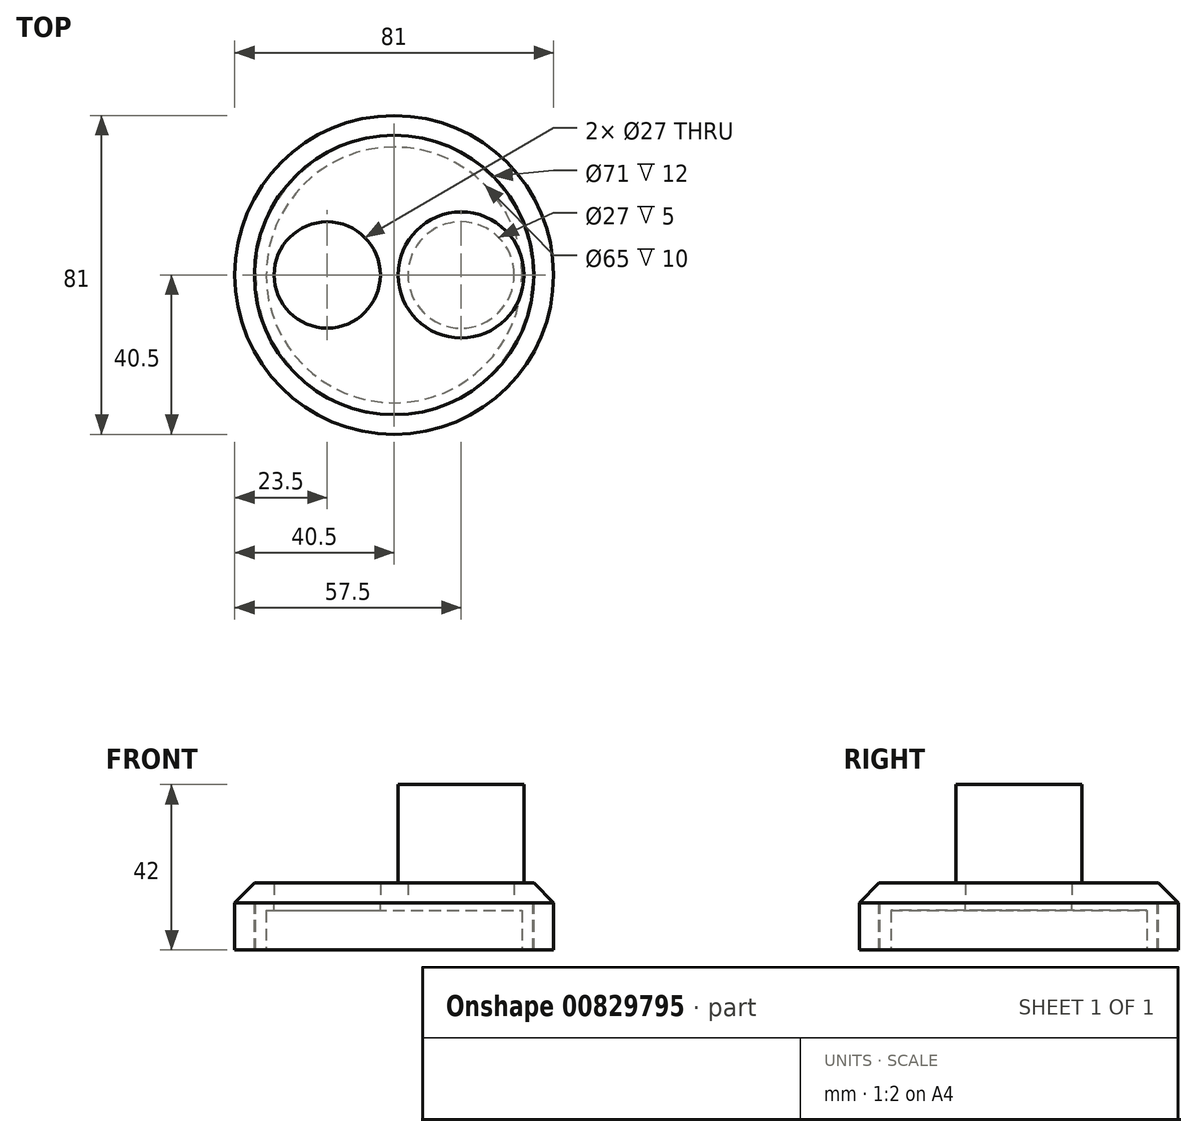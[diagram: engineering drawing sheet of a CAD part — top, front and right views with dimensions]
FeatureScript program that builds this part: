
annotation { "Feature Type Name" : "Feature", "Feature Type Description" : "" }
export const myFeature = defineFeature(function(context is Context, id is Id, definition is map)
    precondition{}
    {
        {
            var Q0;
            Q0=qCreatedBy(makeId("Front.planeOp"),FACE);
            var sketch = newSketch(context, id + "F0", { "sketchPlane" : qUnion([Q0])});
            skLineSegment(sketch, "E0", {"start": v(-40.5, 0) * mm, "end": v(-40.5, 17) * mm});
            skLineSegment(sketch, "E1", {"start": v(-40.5, 17) * mm, "end": v(0, 17) * mm});
            skLineSegment(sketch, "E2", {"start": v(0, 17) * mm, "end": v(0, 12) * mm});
            skLineSegment(sketch, "E3", {"start": v(0, 12) * mm, "end": v(-35.5, 12) * mm});
            skLineSegment(sketch, "E4", {"start": v(-35.5, 12) * mm, "end": v(-35.5, 0) * mm});
            skLineSegment(sketch, "E5", {"start": v(-35.5, 0) * mm, "end": v(-40.5, 0) * mm});
            skSolve(sketch);
        }
        {
            var Q0;
            Q0=makeQuery(id+"F0.imprint","IMPRINT",FACE,{"disambiguationData":[TD([[makeQuery(id+"F0.imprint","IMPRINT",EDGE,{"derivedFrom":sQuery(id+"F0.wireOp",EDGE,"E0")}),-1.0]])]});
            var Q1;
            Q1=sQuery(id+"F0.wireOp",EDGE,"E2");
            revolve(context, id + "F1", {"surfaceOperationType" : NewSurfaceOperationType.NEW, "entities" : qUnion([Q0]), "axis" : qUnion([Q1]), "revolveType" : RevolveType.FULL});
        }
        {
            var Q0;
            Q0=makeQuery(id+"F1.opRevolve","SWEPT_FACE",FACE,{"disambiguationData":[OSD([sQuery(id+"F0.wireOp",EDGE,"E3")])]});
            var sketch = newSketch(context, id + "F2", { "sketchPlane" : qUnion([Q0])});
            skCircle(sketch, "E6", {"center": v(0, 0) * mm, "radius": 17 * mm, "construction": true});
            skLineSegment(sketch, "E7", {"start": v(0, 0) * mm, "end": v(-17, 0) * mm, "construction": true});
            skLineSegment(sketch, "E8", {"start": v(0, 0) * mm, "end": v(0, 17) * mm, "construction": true});
            skCircle(sketch, "E9", {"center": v(-17, 0) * mm, "radius": 13.5 * mm});
            skCircle(sketch, "E10.MirrorC", {"center": v(17, 0) * mm, "radius": 13.5 * mm});
            skSolve(sketch);
        }
        {
            var Q0;
            Q0 = qSketchRegion(id + "F2", true);
            extrude(context, id + "F3", {"entities" : qUnion([Q0]), "operationType" : NewBodyOperationType.REMOVE, "oppositeDirection" : true, "depth" : 25 * mm, "offsetDistance" : 25 * mm});
        }
        {
            var Q0;
            Q0=makeQuery(id+"F1.opRevolve","SWEPT_EDGE",EDGE,{"disambiguationData":[OSD([sQuery(id+"F0.wireOp",EDGE,"E0"),sQuery(id+"F0.wireOp",EDGE,"E1")])]});
            chamfer(context, id + "F4", {"entities" : qUnion([Q0]), "width" : 5 * mm, "tangentPropagation" : true});
        }
        {
            var Q0;
            Q0=makeQuery(id+"F1.opRevolve","SWEPT_FACE",FACE,{"disambiguationData":[OSD([sQuery(id+"F0.wireOp",EDGE,"E3")])]});
            var sketch = newSketch(context, id + "F5", { "sketchPlane" : qUnion([Q0])});
            skCircle(sketch, "E11", {"center": v(0, 0) * mm, "radius": 35.25 * mm});
            skCircle(sketch, "E12.0", {"center": v(-17, 0) * mm, "radius": 13.5 * mm});
            skSolve(sketch);
        }
        {
            var Q0;
            Q0=makeQuery(id+"F5.imprint","IMPRINT",FACE,{"disambiguationData":[TD([[makeQuery(id+"F5.imprint","IMPRINT",EDGE,{"derivedFrom":sQuery(id+"F5.wireOp",EDGE,"E11")}),1.0]])]});
            var Q1;
            Q1 = qSketchRegion(id + "F5", true);
            extrude(context, id + "F6", {"entities" : qUnion([Q0, Q1]), "depth" : 12 * mm, "offsetDistance" : 25 * mm});
        }
        {
            var Q0;
            Q0=makeQuery(id+"F6.opExtrude","CAP_FACE",FACE,{"disambiguationData":[OSD([sQuery(id+"F5.wireOp",EDGE,"E11"),sQuery(id+"F5.wireOp",EDGE,"E12.0")])],"isStart":false});
            var sketch = newSketch(context, id + "F7", { "sketchPlane" : qUnion([Q0])});
            skCircle(sketch, "E13", {"center": v(0, 0) * mm, "radius": 32.5 * mm});
            skSolve(sketch);
        }
        {
            var Q0;
            Q0 = qSketchRegion(id + "F7", true);
            var Q1;
            Q1=makeQuery(id+"F7.imprint","IMPRINT",FACE,{"disambiguationData":[TD([[makeQuery(id+"F7.imprint","IMPRINT",EDGE,{"derivedFrom":sQuery(id+"F7.wireOp",EDGE,"E13")}),1.0]])]});
            extrude(context, id + "F8", {"entities" : qUnion([Q0, Q1]), "operationType" : NewBodyOperationType.REMOVE, "oppositeDirection" : true, "depth" : 10 * mm, "offsetDistance" : 25 * mm});
        }
        {
            var Q0;
            Q0=makeQuery(id+"F1.opRevolve","SWEPT_FACE",FACE,{"disambiguationData":[OSD([sQuery(id+"F0.wireOp",EDGE,"E1")])]});
            var sketch = newSketch(context, id + "F9", { "sketchPlane" : qUnion([Q0])});
            skCircle(sketch, "E14.0", {"center": v(17, 0) * mm, "radius": 13.5 * mm});
            skCircle(sketch, "E15", {"center": v(17, 0) * mm, "radius": 16 * mm});
            skSolve(sketch);
        }
        {
            var Q0;
            Q0=makeQuery(id+"F9.imprint","IMPRINT",FACE,{"disambiguationData":[TD([[makeQuery(id+"F9.imprint","IMPRINT",EDGE,{"derivedFrom":sQuery(id+"F9.wireOp",EDGE,"E14.0")}),-1.0]])]});
            var Q1;
            Q1 = qSketchRegion(id + "F9", true);
            extrude(context, id + "F10", {"entities" : qUnion([Q0, Q1]), "operationType" : NewBodyOperationType.ADD, "depth" : 25 * mm, "offsetDistance" : 25 * mm});
        }
    });
